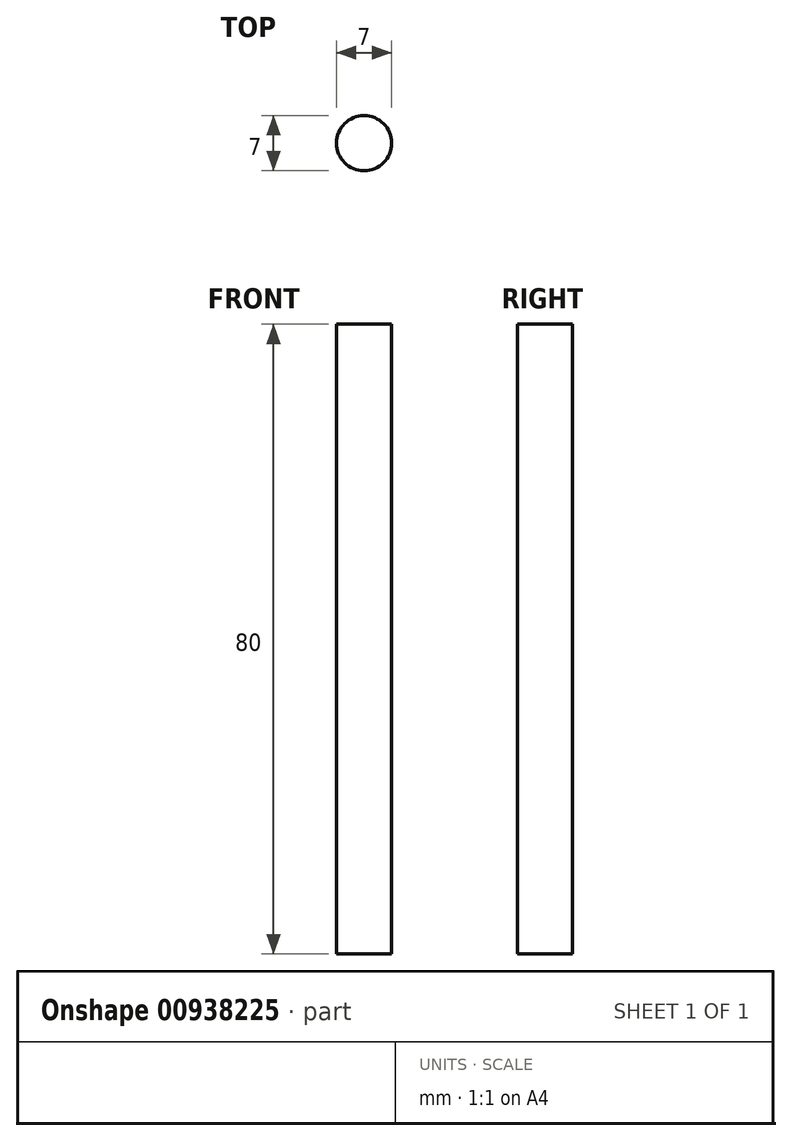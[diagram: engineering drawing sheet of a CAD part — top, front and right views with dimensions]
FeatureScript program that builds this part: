
annotation { "Feature Type Name" : "Feature", "Feature Type Description" : "" }
export const myFeature = defineFeature(function(context is Context, id is Id, definition is map)
    precondition{}
    {
        {
            var Q0;
            Q0=qCreatedBy(makeId("Top.planeOp"),FACE);
            var sketch = newSketch(context, id + "F0", { "sketchPlane" : qUnion([Q0])});
            skCircle(sketch, "E0", {"center": v(0, 0) * mm, "radius": 3.5 * mm});
            skSolve(sketch);
        }
        {
            var Q0;
            Q0=makeQuery(id+"F0.imprint","IMPRINT",FACE,{"disambiguationData":[TD([[makeQuery(id+"F0.imprint","IMPRINT",EDGE,{"derivedFrom":sQuery(id+"F0.wireOp",EDGE,"E0")}),1.0]])]});
            extrude(context, id + "F1", {"entities" : qUnion([Q0]), "depth" : 80 * mm, "offsetDistance" : 25 * mm});
        }
    });
